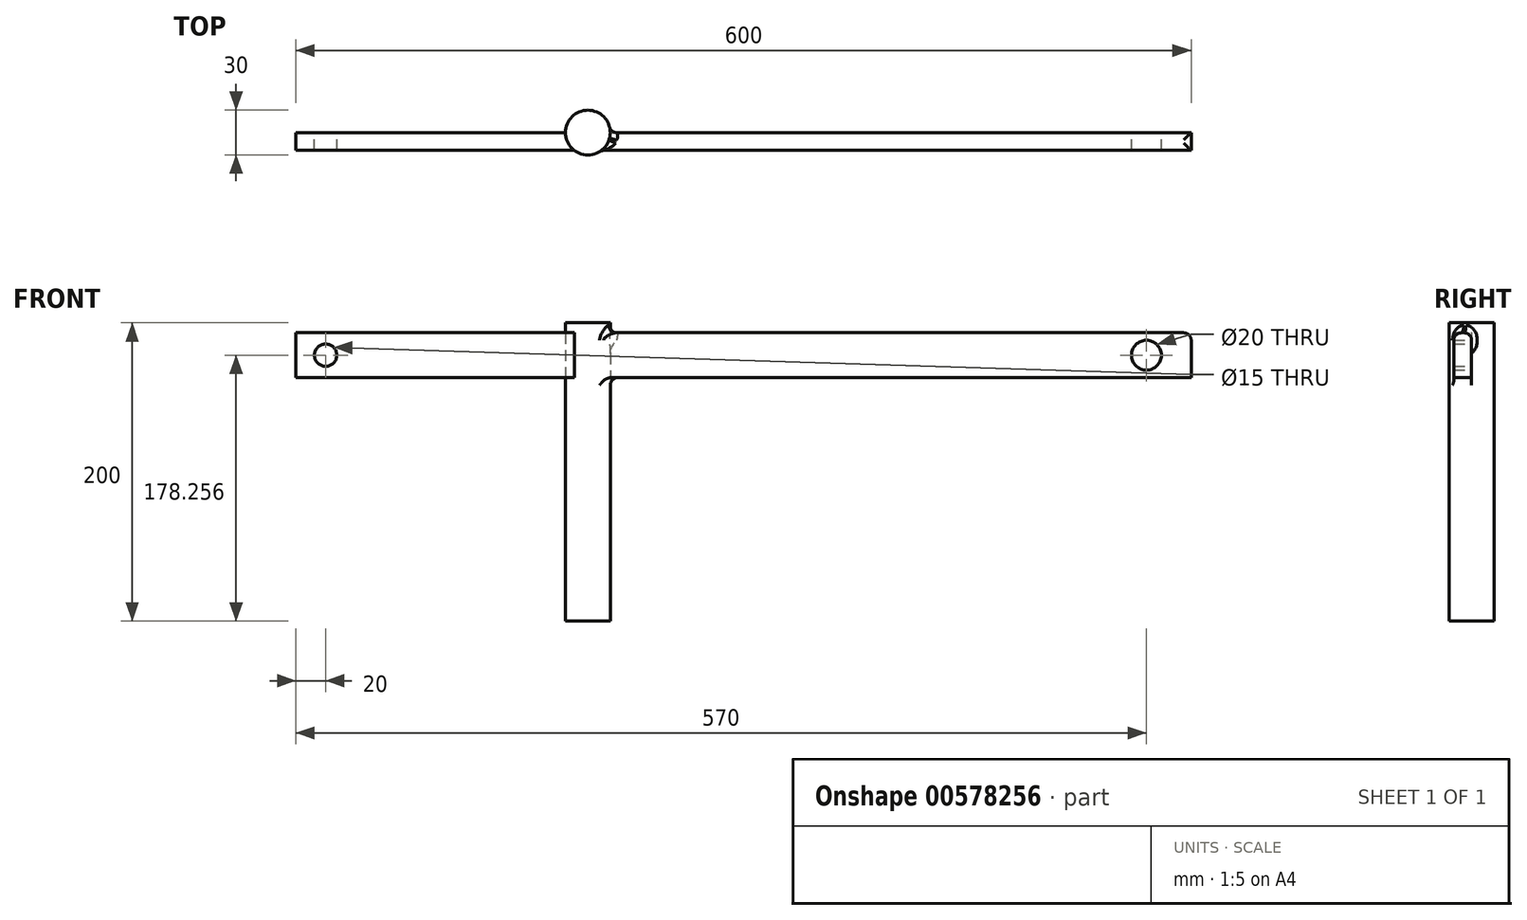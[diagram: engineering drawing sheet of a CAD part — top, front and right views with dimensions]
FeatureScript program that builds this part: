
annotation { "Feature Type Name" : "Feature", "Feature Type Description" : "" }
export const myFeature = defineFeature(function(context is Context, id is Id, definition is map)
    precondition{}
    {
        {
            var Q0;
            Q0=qCreatedBy(makeId("Top.planeOp"),FACE);
            var sketch = newSketch(context, id + "F0", { "sketchPlane" : qUnion([Q0])});
            skCircle(sketch, "E0", {"center": v(0, 0) * mm, "radius": 15 * mm});
            skSolve(sketch);
        }
        {
            var Q0;
            Q0 = qSketchRegion(id + "F0", true);
            extrude(context, id + "F1", {"entities" : qUnion([Q0]), "depth" : 200 * mm, "offsetDistance" : 25 * mm});
        }
        {
            var Q0;
            Q0=qCreatedBy(makeId("Front.planeOp"),FACE);
            var sketch = newSketch(context, id + "F2", { "sketchPlane" : qUnion([Q0])});
            skLineSegment(sketch, "E1.bottom", {"start": v(404.27, 163.26) * mm, "end": v(-195.73, 163.26) * mm});
            skLineSegment(sketch, "E1.top", {"start": v(404.27, 193.26) * mm, "end": v(-195.73, 193.26) * mm});
            skLineSegment(sketch, "E1.left", {"start": v(404.27, 163.26) * mm, "end": v(404.27, 193.26) * mm});
            skLineSegment(sketch, "E1.right", {"start": v(-195.73, 163.26) * mm, "end": v(-195.73, 193.26) * mm});
            skPoint(sketch, "E1.middle", {"position": v(104.27, 178.26) * mm});
            skCircle(sketch, "E2", {"center": v(-175.73, 178.26) * mm, "radius": 7.5 * mm});
            skPoint(sketch, "E2.centerSnap0", {"position": v(-195.73, 178.26) * mm});
            skCircle(sketch, "E3", {"center": v(374.27, 178.26) * mm, "radius": 10 * mm});
            skPoint(sketch, "E3.centerSnap0", {"position": v(404.27, 178.26) * mm});
            skSolve(sketch);
        }
        {
            var Q0;
            Q0=makeQuery(id+"F2.imprint","IMPRINT",FACE,{"disambiguationData":[TD([[makeQuery(id+"F2.imprint","IMPRINT",EDGE,{"derivedFrom":sQuery(id+"F2.wireOp",EDGE,"E1.bottom")}),-1.0]])]});
            extrude(context, id + "F3", {"entities" : qUnion([Q0]), "operationType" : NewBodyOperationType.ADD, "depth" : 12 * mm, "offsetDistance" : 25 * mm});
        }
        {
            var Q0;
            Q0=makeQuery(id+"F3.boolean.opBoolean","INTERSECT",EDGE,{"disambiguationData":[OD(0.0)],"derivedFrom":[makeQuery(id+"F1.opExtrude","SWEPT_FACE",FACE,{"disambiguationData":[OSD([sQuery(id+"F0.wireOp",EDGE,"E0")])]}),makeQuery(id+"F3.opExtrude","CAP_FACE",FACE,{"disambiguationData":[OSD([sQuery(id+"F2.wireOp",EDGE,"E1.bottom"),sQuery(id+"F2.wireOp",EDGE,"E1.top"),sQuery(id+"F2.wireOp",EDGE,"E1.left"),sQuery(id+"F2.wireOp",EDGE,"E1.right"),sQuery(id+"F2.wireOp",EDGE,"E2"),sQuery(id+"F2.wireOp",EDGE,"E3")])],"isStart":false})]});
            var Q1;
            Q1=makeQuery(id+"F3.boolean.opBoolean","INTERSECT",EDGE,{"disambiguationData":[OD(0.0)],"derivedFrom":[makeQuery(id+"F1.opExtrude","SWEPT_FACE",FACE,{"disambiguationData":[OSD([sQuery(id+"F0.wireOp",EDGE,"E0")])]}),makeQuery(id+"F3.opExtrude","SWEPT_FACE",FACE,{"disambiguationData":[OSD([sQuery(id+"F2.wireOp",EDGE,"E1.bottom")])]})]});
            var Q2;
            {var subQ3=sQuery(id+"F2.wireOp",EDGE,"E1.left");var subQ4=sQuery(id+"F2.wireOp",EDGE,"E1.top");Q2=makeQuery(id+"F3.boolean.opBoolean","SPLIT",FACE,{"disambiguationData":[TD([makeQuery(id+"F3.opExtrude","SWEPT_FACE",FACE,{"disambiguationData":[OSD([subQ3])]})])],"derivedFrom":makeQuery(id+"F3.opExtrude","SWEPT_FACE",FACE,{"disambiguationData":[OSD([subQ4])]})});}
            var Q3;
            Q3=makeQuery(id+"F3.boolean.opBoolean","INTERSECT",EDGE,{"disambiguationData":[OD(0.0)],"derivedFrom":[makeQuery(id+"F1.opExtrude","SWEPT_FACE",FACE,{"disambiguationData":[OSD([sQuery(id+"F0.wireOp",EDGE,"E0")])]}),makeQuery(id+"F3.opExtrude","SWEPT_FACE",FACE,{"disambiguationData":[OSD([sQuery(id+"F2.wireOp",EDGE,"E1.top")])]})]});
            fillet(context, id + "F4", {"entities" : qUnion([Q0, Q1, Q2, Q3]), "radius" : 5 * mm, "tangentPropagation" : true, "allowEdgeOverflow" : false});
        }
    });
